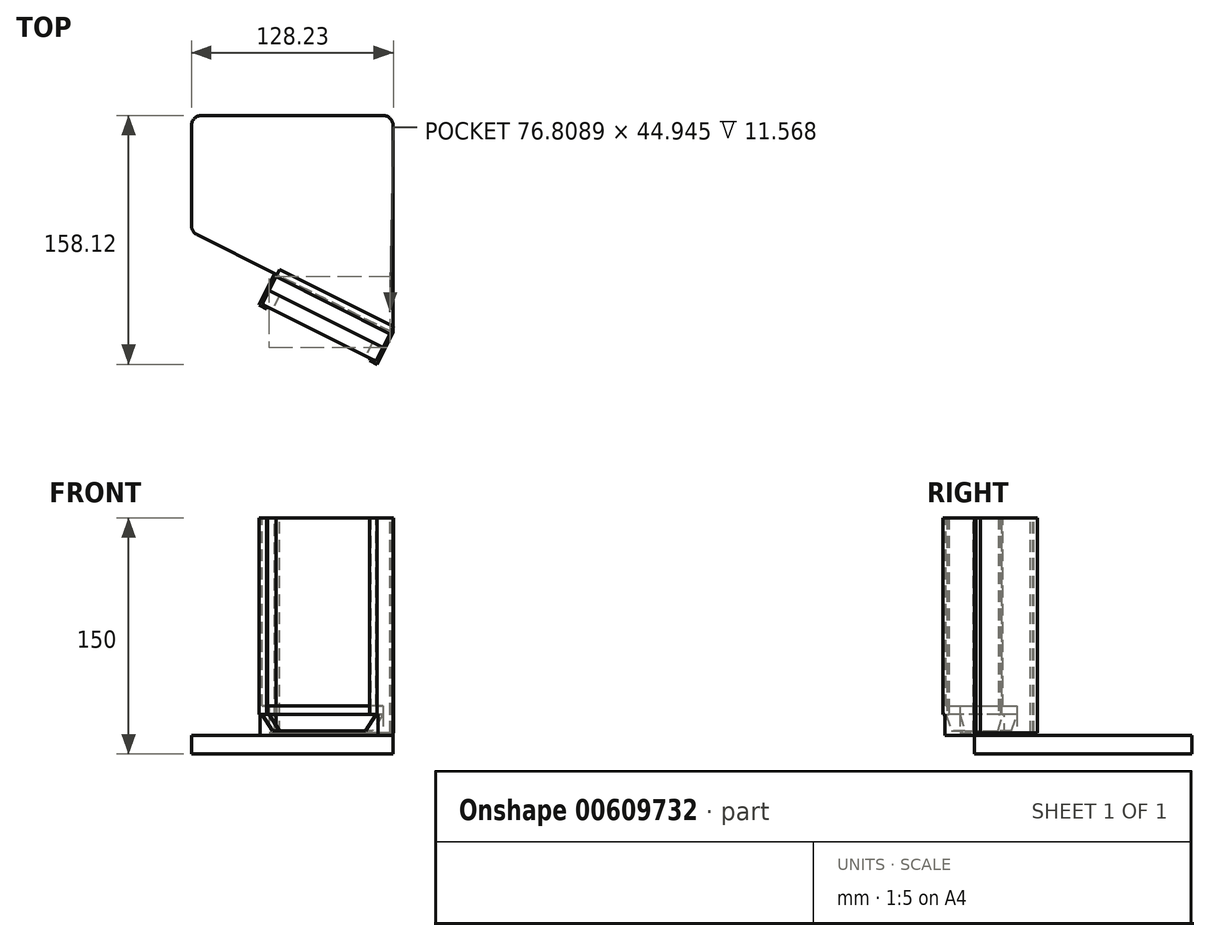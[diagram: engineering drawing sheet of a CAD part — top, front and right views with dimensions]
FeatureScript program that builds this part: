
annotation { "Feature Type Name" : "Feature", "Feature Type Description" : "" }
export const myFeature = defineFeature(function(context is Context, id is Id, definition is map)
    precondition{}
    {
        {
            var Q0;
            Q0=qCreatedBy(makeId("Top.planeOp"),FACE);
            var sketch = newSketch(context, id + "F0", { "sketchPlane" : qUnion([Q0])});
            skLineSegment(sketch, "E0", {"start": v(-58.28, 32.58) * mm, "end": v(57.02, 32.58) * mm});
            skLineSegment(sketch, "E1", {"start": v(63.37, 26.23) * mm, "end": v(63.37, -105.42) * mm});
            skLineSegment(sketch, "E2", {"start": v(63.37, -105.42) * mm, "end": v(-61.12, -43.17) * mm});
            skLineSegment(sketch, "E3", {"start": v(-64.63, -37.5) * mm, "end": v(-64.63, 26.23) * mm});
            skPoint(sketch, "E4.visualSharp", {"position": v(-64.63, 32.58) * mm});
            skArc(sketch, "E4.filletArc", {"start": v(-58.28, 32.58) * mm, "mid": v(-62.77, 30.72) * mm, "end": v(-64.63, 26.23) * mm});
            skPoint(sketch, "E5.visualSharp", {"position": v(63.37, 32.58) * mm});
            skArc(sketch, "E5.filletArc", {"start": v(63.37, 26.23) * mm, "mid": v(61.51, 30.72) * mm, "end": v(57.02, 32.58) * mm});
            skPoint(sketch, "E6.visualSharp", {"position": v(-64.63, -41.42) * mm});
            skArc(sketch, "E6.filletArc", {"start": v(-64.63, -37.5) * mm, "mid": v(-63.68, -40.83) * mm, "end": v(-61.12, -43.17) * mm});
            skSolve(sketch);
        }
        {
            var Q0;
            Q0 = qSketchRegion(id + "F0", true);
            extrude(context, id + "F1", {"entities" : qUnion([Q0]), "depth" : 12 * mm, "offsetDistance" : 25 * mm});
        }
        {
            var Q0;
            Q0=makeQuery(id+"F1.opExtrude","SWEPT_FACE",FACE,{"disambiguationData":[OSD([sQuery(id+"F0.wireOp",EDGE,"E2")])]});
            var sketch = newSketch(context, id + "F2", { "sketchPlane" : qUnion([Q0])});
            skLineSegment(sketch, "E7.bottom", {"start": v(103.83, 0) * mm, "end": v(19.83, 0) * mm});
            skLineSegment(sketch, "E7.top", {"start": v(103.83, 150) * mm, "end": v(19.83, 150) * mm});
            skLineSegment(sketch, "E7.left", {"start": v(103.83, 0) * mm, "end": v(103.83, 150) * mm});
            skLineSegment(sketch, "E7.right", {"start": v(19.83, 0) * mm, "end": v(19.83, 150) * mm});
            skSolve(sketch);
        }
        {
            var Q0;
            {var subQ0=sQuery(id+"F2.wireOp",EDGE,"E7.top");Q0=makeQuery(id+"F2.imprint","IMPRINT",FACE,{"disambiguationData":[TD([[makeQuery(id+"F2.imprint","IMPRINT",EDGE,{"derivedFrom":subQ0}),1.0]])]});}
            extrude(context, id + "F3", {"entities" : qUnion([Q0]), "depth" : 21 * mm, "offsetDistance" : 25 * mm});
        }
        {
            var Q0;
            Q0=makeQuery(id+"F3.opExtrude","CAP_FACE",FACE,{"disambiguationData":[OSD([sQuery(id+"F0.wireOp",EDGE,"E2"),sQuery(id+"F2.wireOp",EDGE,"E7.top"),sQuery(id+"F2.wireOp",EDGE,"E7.left"),sQuery(id+"F2.wireOp",EDGE,"E7.right")])],"isStart":false});
            shell(context, id + "F4", {"entities" : qUnion([Q0]), "thickness" : 1.5 * mm});
        }
        {
            var Q0;
            Q0=makeQuery(id+"F4.opShell","OFFSET_FACE",FACE,{"disambiguationData":[OSD([sQuery(id+"F2.wireOp",EDGE,"E7.top")])]});
            var sketch = newSketch(context, id + "F5", { "sketchPlane" : qUnion([Q0])});
            skLineSegment(sketch, "E8", {"start": v(-11.09, 69.87) * mm, "end": v(61.36, 106.1) * mm});
            skLineSegment(sketch, "E9", {"start": v(61.36, 106.1) * mm, "end": v(52.64, 123.53) * mm});
            skLineSegment(sketch, "E10", {"start": v(52.64, 123.53) * mm, "end": v(-19.81, 87.3) * mm});
            skLineSegment(sketch, "E11", {"start": v(-19.81, 87.3) * mm, "end": v(-11.09, 69.87) * mm});
            skSolve(sketch);
        }
        {
            var Q0;
            Q0 = qSketchRegion(id + "F5", true);
            extrude(context, id + "F6", {"entities" : qUnion([Q0]), "operationType" : NewBodyOperationType.REMOVE, "oppositeDirection" : true, "depth" : 5 * mm, "offsetDistance" : 25 * mm});
        }
        {
            var Q0;
            Q0=makeQuery(id+"F4.opShell","OFFSET_FACE",FACE,{"disambiguationData":[OSD([sQuery(id+"F0.wireOp",EDGE,"E2")])]});
            var sketch = newSketch(context, id + "F7", { "sketchPlane" : qUnion([Q0])});
            skLineSegment(sketch, "E12", {"start": v(57, -114.81) * mm, "end": v(-15.45, -78.59) * mm});
            skLineSegment(sketch, "E13", {"start": v(-15.45, -78.59) * mm, "end": v(-19.81, -87.3) * mm});
            skLineSegment(sketch, "E14", {"start": v(-19.81, -87.3) * mm, "end": v(52.64, -123.53) * mm});
            skLineSegment(sketch, "E15", {"start": v(52.64, -123.53) * mm, "end": v(57, -114.81) * mm});
            skSolve(sketch);
        }
        {
            var Q0;
            Q0 = qSketchRegion(id + "F7", true);
            extrude(context, id + "F8", {"entities" : qUnion([Q0]), "operationType" : NewBodyOperationType.ADD, "depth" : 17 * mm, "offsetDistance" : 25 * mm});
        }
        {
            var Q0;
            Q0=makeQuery(id+"F8.boolean.opBoolean","MERGE",FACE,{"derivedFrom":[makeQuery(id+"F3.opExtrude","CAP_FACE",FACE,{"disambiguationData":[OSD([sQuery(id+"F0.wireOp",EDGE,"E2"),sQuery(id+"F2.wireOp",EDGE,"E7.top"),sQuery(id+"F2.wireOp",EDGE,"E7.left"),sQuery(id+"F2.wireOp",EDGE,"E7.right")])],"isStart":false}),makeQuery(id+"F8.opExtrude","SWEPT_FACE",FACE,{"disambiguationData":[OSD([sQuery(id+"F7.wireOp",EDGE,"E14")])]})]});
            var sketch = newSketch(context, id + "F9", { "sketchPlane" : qUnion([Q0])});
            skLineSegment(sketch, "E16", {"start": v(21.33, 25.07) * mm, "end": v(102.33, 25.07) * mm});
            skLineSegment(sketch, "E17", {"start": v(102.33, 25.07) * mm, "end": v(94.89, 14.8) * mm});
            skLineSegment(sketch, "E18", {"start": v(94.89, 14.8) * mm, "end": v(28.77, 14.8) * mm});
            skLineSegment(sketch, "E19", {"start": v(28.77, 14.8) * mm, "end": v(21.33, 25.07) * mm});
            skSolve(sketch);
        }
        {
            var Q0;
            Q0=makeQuery(id+"F9.imprint","IMPRINT",FACE,{"disambiguationData":[TD([[makeQuery(id+"F9.imprint","IMPRINT",EDGE,{"derivedFrom":sQuery(id+"F9.wireOp",EDGE,"E16")}),-1.0]])]});
            extrude(context, id + "F10", {"entities" : qUnion([Q0]), "operationType" : NewBodyOperationType.REMOVE, "oppositeDirection" : true, "depth" : 15 * mm, "offsetDistance" : 25 * mm});
        }
        {
            var Q0;
            Q0=makeQuery(id+"F6.boolean.opBoolean","MERGE",FACE,{"derivedFrom":[makeQuery(id+"F4.opShell","OFFSET_FACE",FACE,{"disambiguationData":[OSD([sQuery(id+"F0.wireOp",EDGE,"E2"),sQuery(id+"F2.wireOp",EDGE,"E7.top"),sQuery(id+"F2.wireOp",EDGE,"E7.left"),sQuery(id+"F2.wireOp",EDGE,"E7.right")])]}),makeQuery(id+"F6.opExtrude","SWEPT_FACE",FACE,{"disambiguationData":[OSD([sQuery(id+"F5.wireOp",EDGE,"E8")])]})]});
            extrude(context, id + "F11", {"entities" : qUnion([Q0]), "operationType" : NewBodyOperationType.ADD, "oppositeDirection" : true, "depth" : 5 * mm, "offsetDistance" : 25 * mm});
        }
        {
            var Q0;
            Q0=makeQuery(id+"F8.boolean.opBoolean","MERGE",FACE,{"derivedFrom":[makeQuery(id+"F3.opExtrude","CAP_FACE",FACE,{"disambiguationData":[OSD([sQuery(id+"F0.wireOp",EDGE,"E2"),sQuery(id+"F2.wireOp",EDGE,"E7.top"),sQuery(id+"F2.wireOp",EDGE,"E7.left"),sQuery(id+"F2.wireOp",EDGE,"E7.right")])],"isStart":false}),makeQuery(id+"F8.opExtrude","SWEPT_FACE",FACE,{"disambiguationData":[OSD([sQuery(id+"F7.wireOp",EDGE,"E14")])]})]});
            var sketch = newSketch(context, id + "F12", { "sketchPlane" : qUnion([Q0])});
            skLineSegment(sketch, "E20.bottom", {"start": v(103.83, 150) * mm, "end": v(98.33, 150) * mm});
            skLineSegment(sketch, "E20.top", {"start": v(103.83, 25.07) * mm, "end": v(98.33, 25.07) * mm});
            skLineSegment(sketch, "E20.left", {"start": v(103.83, 150) * mm, "end": v(103.83, 25.07) * mm});
            skLineSegment(sketch, "E20.right", {"start": v(98.33, 150) * mm, "end": v(98.33, 25.07) * mm});
            skSolve(sketch);
        }
        {
            var Q0;
            Q0 = qSketchRegion(id + "F12", true);
            extrude(context, id + "F13", {"entities" : qUnion([Q0]), "operationType" : NewBodyOperationType.ADD, "depth" : 1.5 * mm, "offsetDistance" : 25 * mm});
        }
        {
            var Q0;
            Q0=makeQuery(id+"F8.boolean.opBoolean","MERGE",FACE,{"derivedFrom":[makeQuery(id+"F3.opExtrude","CAP_FACE",FACE,{"disambiguationData":[OSD([sQuery(id+"F0.wireOp",EDGE,"E2"),sQuery(id+"F2.wireOp",EDGE,"E7.top"),sQuery(id+"F2.wireOp",EDGE,"E7.left"),sQuery(id+"F2.wireOp",EDGE,"E7.right")])],"isStart":false}),makeQuery(id+"F8.opExtrude","SWEPT_FACE",FACE,{"disambiguationData":[OSD([sQuery(id+"F7.wireOp",EDGE,"E14")])]})]});
            var sketch = newSketch(context, id + "F14", { "sketchPlane" : qUnion([Q0])});
            skLineSegment(sketch, "E21.bottom", {"start": v(19.83, 150) * mm, "end": v(25.33, 150) * mm});
            skLineSegment(sketch, "E21.top", {"start": v(19.83, 25.07) * mm, "end": v(25.33, 25.07) * mm});
            skLineSegment(sketch, "E21.left", {"start": v(19.83, 150) * mm, "end": v(19.83, 25.07) * mm});
            skLineSegment(sketch, "E21.right", {"start": v(25.33, 150) * mm, "end": v(25.33, 25.07) * mm});
            skSolve(sketch);
        }
        {
            var Q0;
            Q0 = qSketchRegion(id + "F14", true);
            extrude(context, id + "F15", {"entities" : qUnion([Q0]), "operationType" : NewBodyOperationType.ADD, "depth" : 1.5 * mm, "offsetDistance" : 25 * mm});
        }
    });
